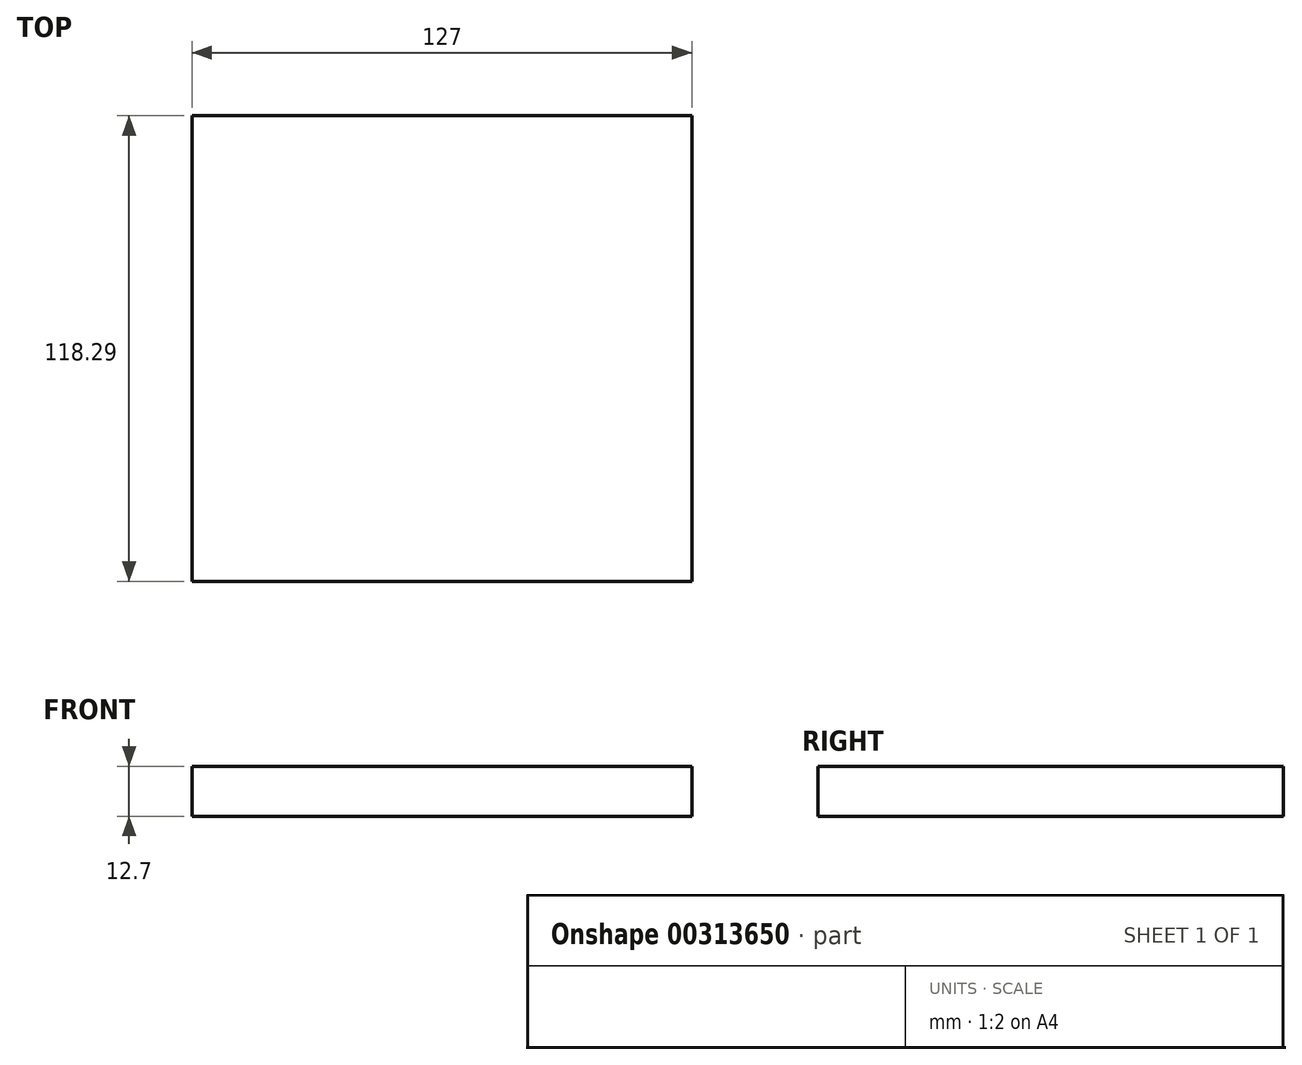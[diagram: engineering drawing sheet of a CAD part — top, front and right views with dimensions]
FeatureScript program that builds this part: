
annotation { "Feature Type Name" : "Feature", "Feature Type Description" : "" }
export const myFeature = defineFeature(function(context is Context, id is Id, definition is map)
    precondition{}
    {
        {
            var Q0;
            Q0=qCreatedBy(makeId("Top.planeOp"),FACE);
            var sketch = newSketch(context, id + "F0", { "sketchPlane" : qUnion([Q0])});
            skLineSegment(sketch, "E0.bottom", {"start": v(0, 0) * mm, "end": v(127, 0) * mm});
            skLineSegment(sketch, "E0.top", {"start": v(0, -118.29) * mm, "end": v(127, -118.29) * mm});
            skLineSegment(sketch, "E0.left", {"start": v(0, 0) * mm, "end": v(0, -118.29) * mm});
            skLineSegment(sketch, "E0.right", {"start": v(127, 0) * mm, "end": v(127, -118.29) * mm});
            skLineSegment(sketch, "E1", {"start": v(0, -118.29) * mm, "end": v(0, -92.89) * mm});
            skSolve(sketch);
        }
        {
            var Q0;
            Q0=makeQuery(id+"F0.imprint","IMPRINT",FACE,{"disambiguationData":[TD([[makeQuery(id+"F0.imprint","IMPRINT",EDGE,{"derivedFrom":sQuery(id+"F0.wireOp",EDGE,"E0.bottom")}),-1.0]])]});
            extrude(context, id + "F1", {"entities" : qUnion([Q0]), "depth" : 12.7 * mm});
        }
    });
